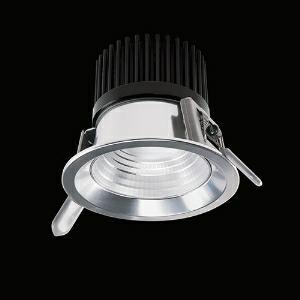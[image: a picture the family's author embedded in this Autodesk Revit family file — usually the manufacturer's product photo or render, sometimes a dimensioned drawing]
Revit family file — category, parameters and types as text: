
# Revit family: spectral_myral_myral_3500-840-s
name_source: partatom
category: Lighting Fixtures
revit_build: Autodesk Revit 2016 (Build: 20150220_1215(x64)
units: mm (PartAtom-declared; Revit-internal decimal feet)

## family parameters
Cut with Voids When Loaded = No
Host = Face
Light Source = No
Part Type = Normal
Room Calculation Point = No
Round Connector Dimension = Use Diameter
Shared = No

## types (1)
- SPECTRAL MYRAL (1 x )
    Apparent Load = 0 VA
    Approval mark = CE
    CIE Flux Codes = 85 100 100 100 100
    Control Gear = Electronic transformer
    Default Elevation = 1800 mm
    Description = SPG0320175
MYRAL recessed spot

Design:
    Height = 0 mm  [stored 0 ft]
    Lamp = 1 x
    Lamp count = 1
    Length = 120 mm
    Luminous efficacy = 0 lm/W
    Manufacturer = Ridi
    ModVariant = No
    Model = MYRAL 3500-840-S
    Mounting Place = Ceiling
    Mounting Type = Recessed
    Number of Poles = 1
    OnlyDefault = Yes
    Power Factor = 1
    Product Name = SPECTRAL MYRAL
    Product group = Downlight recessed
    ProductGroupID = 400
    Protection Class = Protection class
    Protection Degree = IP 20
    RlxData = <blob elided: 38897 chars, md5=ad27cf7b>
    Socket = socket
    Standby Power = 0 W
    System Light Flux = 0 lm
    System Power = 0 W
    Type Image = myral_04.jpg
    URL = http://reluxnet.relux.com
    VarID = ---
    Voltage = 0 V
    Weight = 0.00 kg
    Width = 0 mm  [stored 0 ft]

note: [stored X ft] marks values corroborated as IEEE doubles in the binary element streams (Revit-internal decimal feet)

## geometry (parser evidence)
native form markers: Sweep x9
no freeform markers — native parametric forms only
